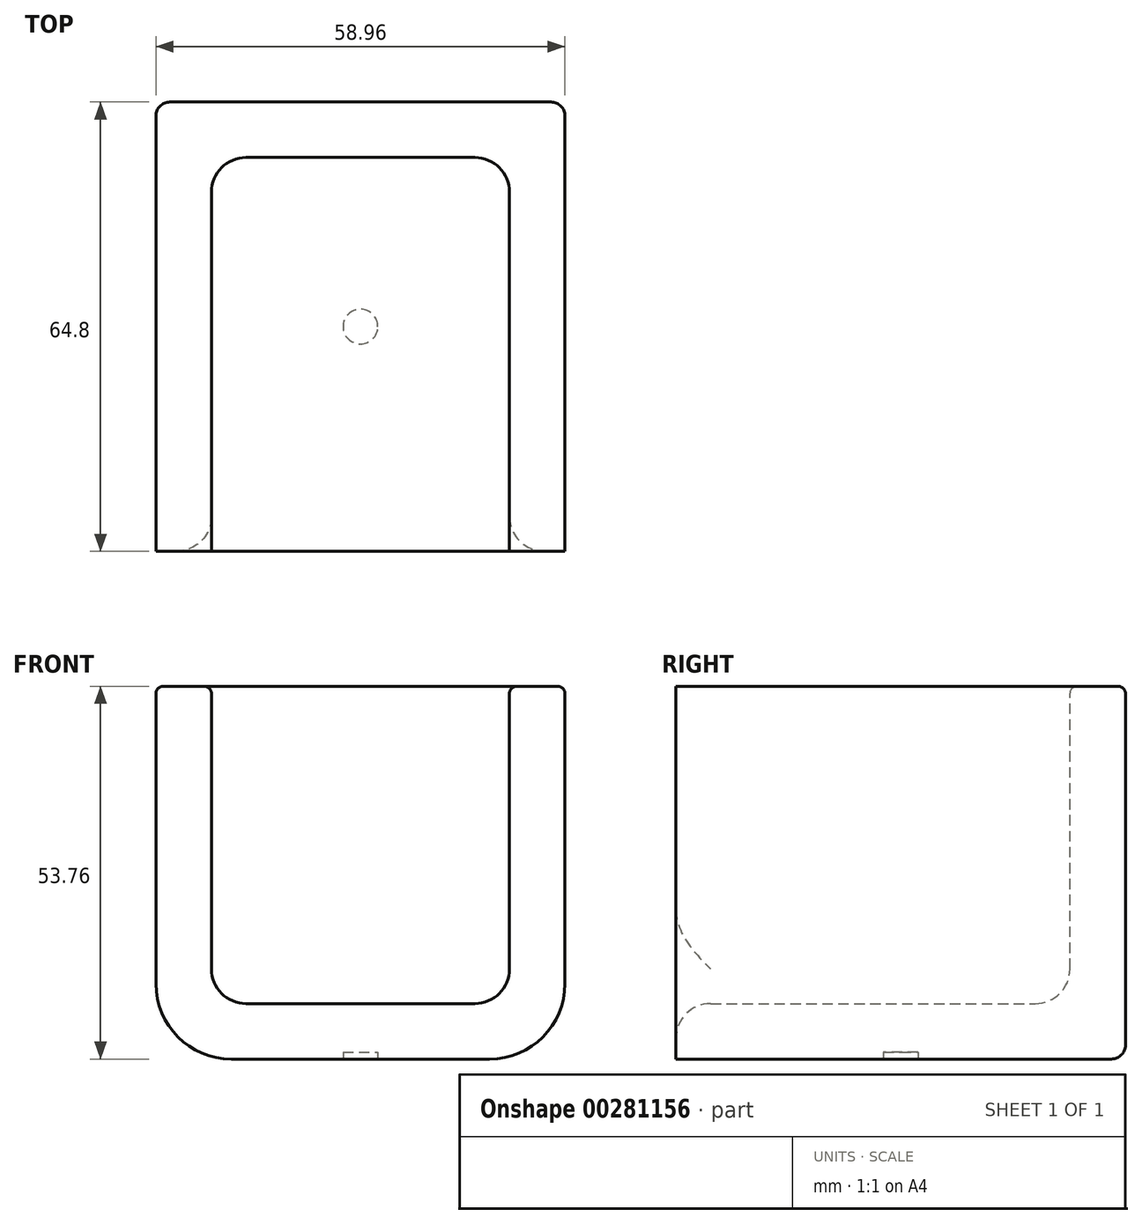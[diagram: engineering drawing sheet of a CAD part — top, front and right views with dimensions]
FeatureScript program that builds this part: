
annotation { "Feature Type Name" : "Feature", "Feature Type Description" : "" }
export const myFeature = defineFeature(function(context is Context, id is Id, definition is map)
    precondition{}
    {
        {
            var Q0;
            Q0=qCreatedBy(makeId("Front.planeOp"),FACE);
            var sketch = newSketch(context, id + "F0", { "sketchPlane" : qUnion([Q0])});
            skLineSegment(sketch, "E0.bottom", {"start": v(29.48, -26.88) * mm, "end": v(-29.48, -26.88) * mm});
            skLineSegment(sketch, "E0.top", {"start": v(29.48, 26.88) * mm, "end": v(-29.48, 26.88) * mm});
            skLineSegment(sketch, "E0.left", {"start": v(29.48, -26.88) * mm, "end": v(29.48, 26.88) * mm});
            skLineSegment(sketch, "E0.right", {"start": v(-29.48, -26.88) * mm, "end": v(-29.48, 26.88) * mm});
            skPoint(sketch, "E0.middle", {"position": v(0, 0) * mm});
            skSolve(sketch);
        }
        {
            var Q0;
            Q0=makeQuery(id+"F0.imprint","IMPRINT",FACE,{"disambiguationData":[TD([[makeQuery(id+"F0.imprint","IMPRINT",EDGE,{"derivedFrom":sQuery(id+"F0.wireOp",EDGE,"E0.bottom")}),-1.0]])]});
            extrude(context, id + "F1", {"entities" : qUnion([Q0]), "endBound" : BoundingType.SYMMETRIC, "depth" : 64.8 * mm});
        }
        {
            var Q0;
            Q0=makeQuery(id+"F1.opExtrude","SWEPT_FACE",FACE,{"disambiguationData":[OSD([sQuery(id+"F0.wireOp",EDGE,"E0.top")])]});
            var Q1;
            Q1=makeQuery(id+"F1.opExtrude","CAP_FACE",FACE,{"disambiguationData":[OSD([sQuery(id+"F0.wireOp",EDGE,"E0.bottom"),sQuery(id+"F0.wireOp",EDGE,"E0.top"),sQuery(id+"F0.wireOp",EDGE,"E0.left"),sQuery(id+"F0.wireOp",EDGE,"E0.right")])],"isStart":false});
            shell(context, id + "F2", {"entities" : qUnion([Q0, Q1]), "thickness" : 8 * mm});
        }
        {
            var Q0;
            {var subQ0=sQuery(id+"F0.wireOp",EDGE,"E0.bottom");Q0=makeQuery(id+"F2.opShell","OFFSET_EDGE",EDGE,{"disambiguationData":[OSD([subQ0]),TDD([makeQuery(id+"F1.opExtrude","CAP_EDGE",EDGE,{"disambiguationData":[OSD([subQ0])],"isStart":true})])]});}
            var Q1;
            Q1=makeQuery(id+"F2.opShell","OFFSET_FACE",FACE,{"disambiguationData":[OSD([sQuery(id+"F0.wireOp",EDGE,"E0.bottom")])]});
            var Q2;
            {var subQ0=sQuery(id+"F0.wireOp",EDGE,"E0.right");Q2=makeQuery(id+"F2.opShell","OFFSET_EDGE",EDGE,{"disambiguationData":[OSD([subQ0]),TDD([makeQuery(id+"F1.opExtrude","CAP_EDGE",EDGE,{"disambiguationData":[OSD([subQ0])],"isStart":true})])]});}
            var Q3;
            {var subQ0=sQuery(id+"F0.wireOp",EDGE,"E0.left");Q3=makeQuery(id+"F2.opShell","OFFSET_EDGE",EDGE,{"disambiguationData":[OSD([subQ0]),TDD([makeQuery(id+"F1.opExtrude","CAP_EDGE",EDGE,{"disambiguationData":[OSD([subQ0])],"isStart":true})])]});}
            fillet(context, id + "F3", {"entities" : qUnion([Q0, Q1, Q2, Q3]), "radius" : 5 * mm, "tangentPropagation" : true, "allowEdgeOverflow" : false});
        }
        {
            var Q0;
            Q0=makeQuery(id+"F1.opExtrude","SWEPT_EDGE",EDGE,{"disambiguationData":[OSD([sQuery(id+"F0.wireOp",EDGE,"E0.bottom"),sQuery(id+"F0.wireOp",EDGE,"E0.left")])]});
            var Q1;
            Q1=makeQuery(id+"F1.opExtrude","SWEPT_EDGE",EDGE,{"disambiguationData":[OSD([sQuery(id+"F0.wireOp",EDGE,"E0.bottom"),sQuery(id+"F0.wireOp",EDGE,"E0.right")])]});
            fillet(context, id + "F4", {"entities" : qUnion([Q0, Q1]), "radius" : 10.86 * mm, "tangentPropagation" : true, "allowEdgeOverflow" : false});
        }
        {
            var Q0;
            Q0=makeQuery(id+"F1.opExtrude","CAP_EDGE",EDGE,{"disambiguationData":[OSD([sQuery(id+"F0.wireOp",EDGE,"E0.bottom")])],"isStart":true});
            fillet(context, id + "F5", {"entities" : qUnion([Q0]), "radius" : 2 * mm, "tangentPropagation" : true, "allowEdgeOverflow" : false});
        }
        {
            var Q0;
            Q0=makeQuery(id+"FYjio5SGskQc77K_1.boolean.opBoolean","COPY",EDGE,{"derivedFrom":makeQuery(id+"FYjio5SGskQc77K_1.opExtrude","CAP_EDGE",EDGE,{"disambiguationData":[OSD([sQuery(id+"FGytyZUFDc1vXKr_1.wireOp",EDGE,"UN3AVH0u-0Aml-WNJ7-Brjp-RQZDiJ86QmAC")])],"isStart":true})});
            var Q1;
            Q1=makeQuery(id+"FYjio5SGskQc77K_1.boolean.opBoolean","INTERSECT",EDGE,{"derivedFrom":[makeQuery(id+"F2.opShell","OFFSET_FACE",FACE,{"disambiguationData":[OSD([sQuery(id+"F0.wireOp",EDGE,"E0.right")])]}),makeQuery(id+"FYjio5SGskQc77K_1.opExtrude","SWEPT_FACE",FACE,{"disambiguationData":[OSD([sQuery(id+"FGytyZUFDc1vXKr_1.wireOp",EDGE,"UN3AVH0u-0Aml-WNJ7-Brjp-RQZDiJ86QmAC")])]})]});
            var Q2;
            Q2=makeQuery(id+"FYjio5SGskQc77K_1.boolean.opBoolean","INTERSECT",EDGE,{"derivedFrom":[makeQuery(id+"F2.opShell","OFFSET_FACE",FACE,{"disambiguationData":[OSD([sQuery(id+"F0.wireOp",EDGE,"E0.left")])]}),makeQuery(id+"FYjio5SGskQc77K_1.opExtrude","SWEPT_FACE",FACE,{"disambiguationData":[OSD([sQuery(id+"FGytyZUFDc1vXKr_1.wireOp",EDGE,"UN3AVH0u-0Aml-WNJ7-Brjp-RQZDiJ86QmAC")])]})]});
            var Q3;
            Q3=makeQuery(id+"FYjio5SGskQc77K_1.boolean.opBoolean","INTERSECT",EDGE,{"derivedFrom":[makeQuery(id+"F1.opExtrude","SWEPT_FACE",FACE,{"disambiguationData":[OSD([sQuery(id+"F0.wireOp",EDGE,"E0.right")])]}),makeQuery(id+"FYjio5SGskQc77K_1.opExtrude","SWEPT_FACE",FACE,{"disambiguationData":[OSD([sQuery(id+"FGytyZUFDc1vXKr_1.wireOp",EDGE,"sga7xVZX-zVeb-mGox-bYIu-GsVgVryKoDDi")])]})]});
            var Q4;
            {var subQ0=sQuery(id+"F0.wireOp",EDGE,"E0.top");Q4=makeQuery(id+"F2.opShell","OFFSET_EDGE",EDGE,{"disambiguationData":[OSD([subQ0]),TDD([makeQuery(id+"F1.opExtrude","CAP_EDGE",EDGE,{"disambiguationData":[OSD([subQ0])],"isStart":true})])]});}
            var Q5;
            Q5=makeQuery(id+"FYjio5SGskQc77K_1.boolean.opBoolean","INTERSECT",EDGE,{"disambiguationData":[OD(0.0)],"derivedFrom":[makeQuery(id+"F1.opExtrude","SWEPT_FACE",FACE,{"disambiguationData":[OSD([sQuery(id+"F0.wireOp",EDGE,"E0.top")])]}),makeQuery(id+"FYjio5SGskQc77K_1.opExtrude","SWEPT_FACE",FACE,{"disambiguationData":[OSD([sQuery(id+"FGytyZUFDc1vXKr_1.wireOp",EDGE,"02bWZBOe-cdmR-t9rS-Tu2P-OseYX5dkRqKF")])]})]});
            var Q6;
            Q6=makeQuery(id+"FYjio5SGskQc77K_1.boolean.opBoolean","INTERSECT",EDGE,{"disambiguationData":[OD(1.0)],"derivedFrom":[makeQuery(id+"F1.opExtrude","SWEPT_FACE",FACE,{"disambiguationData":[OSD([sQuery(id+"F0.wireOp",EDGE,"E0.top")])]}),makeQuery(id+"FYjio5SGskQc77K_1.opExtrude","SWEPT_FACE",FACE,{"disambiguationData":[OSD([sQuery(id+"FGytyZUFDc1vXKr_1.wireOp",EDGE,"02bWZBOe-cdmR-t9rS-Tu2P-OseYX5dkRqKF")])]})]});
            var Q7;
            Q7=makeQuery(id+"F1.opExtrude","SWEPT_EDGE",EDGE,{"disambiguationData":[OSD([sQuery(id+"F0.wireOp",EDGE,"E0.top"),sQuery(id+"F0.wireOp",EDGE,"E0.left")])]});
            fillet(context, id + "F6", {"entities" : qUnion([Q0, Q1, Q2, Q3, Q4, Q5, Q6, Q7]), "radius" : 1 * mm, "tangentPropagation" : true, "allowEdgeOverflow" : false});
        }
        {
            var Q0;
            Q0=makeQuery(id+"F1.opExtrude","SWEPT_FACE",FACE,{"disambiguationData":[OSD([sQuery(id+"F0.wireOp",EDGE,"E0.bottom")])]});
            var sketch = newSketch(context, id + "F7", { "sketchPlane" : qUnion([Q0])});
            skCircle(sketch, "E1", {"center": v(0, 0) * mm, "radius": 2.5 * mm});
            skSolve(sketch);
        }
        {
            var Q0;
            Q0 = qSketchRegion(id + "F7", true);
            extrude(context, id + "F8", {"entities" : qUnion([Q0]), "operationType" : NewBodyOperationType.REMOVE, "oppositeDirection" : true, "depth" : 1 * mm});
        }
    });
